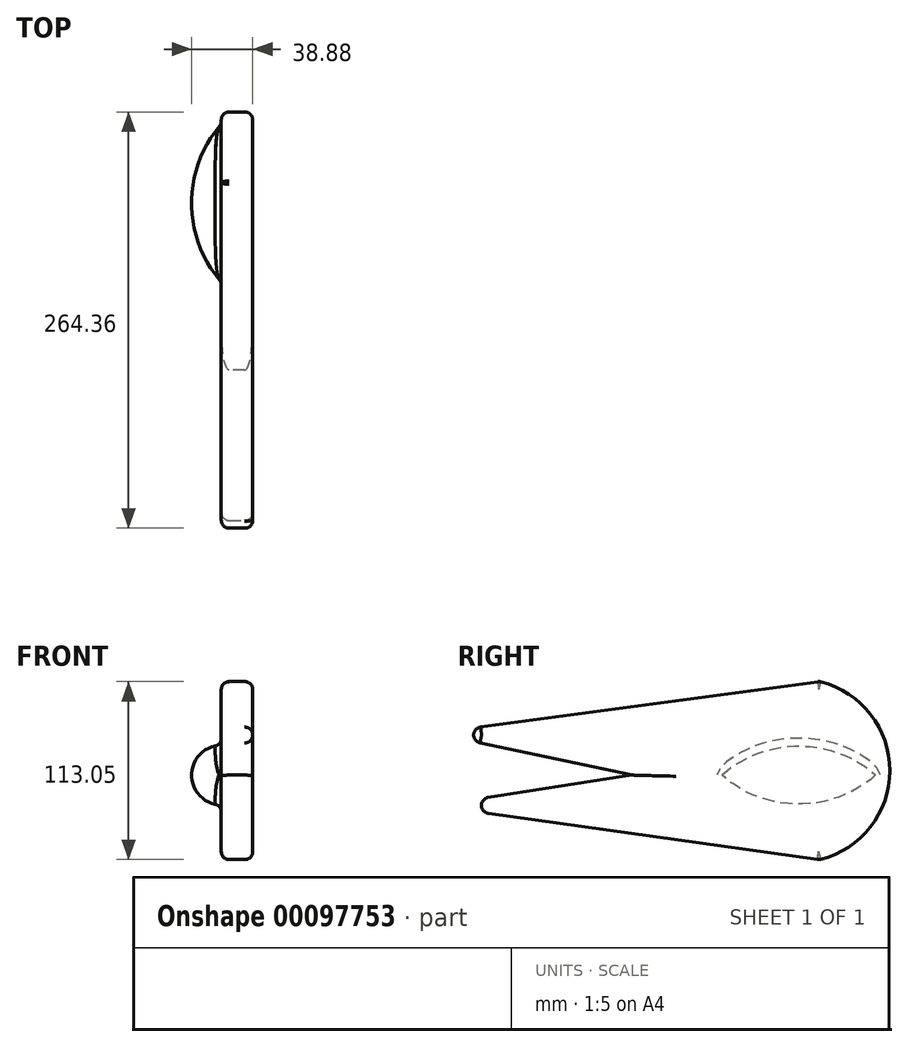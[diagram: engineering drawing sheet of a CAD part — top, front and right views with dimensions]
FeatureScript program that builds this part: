
annotation { "Feature Type Name" : "Feature", "Feature Type Description" : "" }
export const myFeature = defineFeature(function(context is Context, id is Id, definition is map)
    precondition{}
    {
        {
            var Q0;
            Q0=qCreatedBy(makeId("Right.planeOp"),FACE);
            var sketch = newSketch(context, id + "F0", { "sketchPlane" : qUnion([Q0])});
            skLineSegment(sketch, "E0", {"start": v(118.87, -53.77) * mm, "end": v(-125.11, -19.52) * mm});
            skLineSegment(sketch, "E1", {"start": v(119.06, 59.45) * mm, "end": v(-125.11, 26.58) * mm});
            skLineSegment(sketch, "E2", {"start": v(-125.11, 26.58) * mm, "end": v(0, 0) * mm});
            skLineSegment(sketch, "E3", {"start": v(0, 0) * mm, "end": v(-125.11, -19.52) * mm});
            skArc(sketch, "E4", {"start": v(118.87, -53.77) * mm, "mid": v(163.9, 2.76) * mm, "end": v(119.06, 59.45) * mm});
            skSolve(sketch);
        }
        {
            var Q0;
            Q0=makeQuery(id+"F0.imprint","IMPRINT",FACE,{"disambiguationData":[TD([[makeQuery(id+"F0.imprint","IMPRINT",EDGE,{"derivedFrom":sQuery(id+"F0.wireOp",EDGE,"E0")}),-1.0]])]});
            extrude(context, id + "F1", {"entities" : qUnion([Q0]), "depth" : 20 * mm});
        }
        {
            var Q0;
            Q0=makeQuery(id+"F1.opExtrude","SWEPT_EDGE",EDGE,{"disambiguationData":[OSD([sQuery(id+"F0.wireOp",EDGE,"E0"),sQuery(id+"F0.wireOp",EDGE,"E3")])]});
            var Q1;
            Q1=makeQuery(id+"F1.opExtrude","SWEPT_EDGE",EDGE,{"disambiguationData":[OSD([sQuery(id+"F0.wireOp",EDGE,"E1"),sQuery(id+"F0.wireOp",EDGE,"E2")])]});
            var Q2;
            Q2=makeQuery(id+"F1.opExtrude","CAP_EDGE",EDGE,{"disambiguationData":[OSD([sQuery(id+"F0.wireOp",EDGE,"E1")])],"isStart":true});
            var Q3;
            Q3=makeQuery(id+"F1.opExtrude","CAP_EDGE",EDGE,{"disambiguationData":[OSD([sQuery(id+"F0.wireOp",EDGE,"E2")])],"isStart":true});
            var Q4;
            Q4=makeQuery(id+"F1.opExtrude","CAP_EDGE",EDGE,{"disambiguationData":[OSD([sQuery(id+"F0.wireOp",EDGE,"E3")])],"isStart":true});
            var Q5;
            Q5=makeQuery(id+"F1.opExtrude","CAP_EDGE",EDGE,{"disambiguationData":[OSD([sQuery(id+"F0.wireOp",EDGE,"E0")])],"isStart":true});
            var Q6;
            Q6=makeQuery(id+"F1.opExtrude","CAP_EDGE",EDGE,{"disambiguationData":[OSD([sQuery(id+"F0.wireOp",EDGE,"E3")])],"isStart":false});
            var Q7;
            Q7=makeQuery(id+"F1.opExtrude","CAP_EDGE",EDGE,{"disambiguationData":[OSD([sQuery(id+"F0.wireOp",EDGE,"E1")])],"isStart":false});
            var Q8;
            Q8=makeQuery(id+"F1.opExtrude","CAP_EDGE",EDGE,{"disambiguationData":[OSD([sQuery(id+"F0.wireOp",EDGE,"E0")])],"isStart":false});
            var Q9;
            Q9=makeQuery(id+"F1.opExtrude","CAP_EDGE",EDGE,{"disambiguationData":[OSD([sQuery(id+"F0.wireOp",EDGE,"E4")])],"isStart":false});
            var Q10;
            Q10=makeQuery(id+"F1.opExtrude","SWEPT_EDGE",EDGE,{"disambiguationData":[OSD([sQuery(id+"F0.wireOp",EDGE,"E0"),sQuery(id+"F0.wireOp",EDGE,"E4")])]});
            var Q11;
            Q11=makeQuery(id+"F1.opExtrude","SWEPT_EDGE",EDGE,{"disambiguationData":[OSD([sQuery(id+"F0.wireOp",EDGE,"E1"),sQuery(id+"F0.wireOp",EDGE,"E4")])]});
            fillet(context, id + "F2", {"entities" : qUnion([Q0, Q1, Q2, Q3, Q4, Q5, Q6, Q7, Q8, Q9, Q10, Q11]), "radius" : 5.08 * mm, "tangentPropagation" : true, "allowEdgeOverflow" : false});
        }
        {
            var Q0;
            Q0=makeQuery(id+"F1.opExtrude","CAP_FACE",FACE,{"disambiguationData":[OSD([sQuery(id+"F0.wireOp",EDGE,"E0"),sQuery(id+"F0.wireOp",EDGE,"E1"),sQuery(id+"F0.wireOp",EDGE,"E2"),sQuery(id+"F0.wireOp",EDGE,"E3"),sQuery(id+"F0.wireOp",EDGE,"E4")])],"isStart":true});
            var sketch = newSketch(context, id + "F3", { "sketchPlane" : qUnion([Q0])});
            skArc(sketch, "E5", {"start": v(-156.16, 0) * mm, "mid": v(-106.02, -18.88) * mm, "end": v(-55.88, 0) * mm});
            skLineSegment(sketch, "E6", {"start": v(-156.16, 0) * mm, "end": v(-55.88, 0) * mm});
            skSolve(sketch);
        }
        {
            var Q0;
            Q0=makeQuery(id+"F3.imprint","IMPRINT",FACE,{"disambiguationData":[TD([[makeQuery(id+"F3.imprint","IMPRINT",EDGE,{"derivedFrom":sQuery(id+"F3.wireOp",EDGE,"E5")}),1.0]])]});
            var Q1;
            Q1=sQuery(id+"F3.wireOp",EDGE,"E6");
            revolve(context, id + "F4", {"operationType" : NewBodyOperationType.ADD, "entities" : qUnion([Q0]), "axis" : qUnion([Q1]), "revolveType" : RevolveType.ONE_DIRECTION, "oppositeDirection" : true, "angle" : 180 * degree});
        }
        {
            var Q0;
            Q0=makeQuery(id+"F4.opRevolve","CAP_EDGE",EDGE,{"disambiguationData":[OSD([sQuery(id+"F3.wireOp",EDGE,"E5")])],"isStart":false});
            var Q1;
            Q1=makeQuery(id+"F4.opRevolve","CAP_EDGE",EDGE,{"disambiguationData":[OSD([sQuery(id+"F3.wireOp",EDGE,"E5")])],"isStart":true});
            var Q2;
            Q2=makeQuery(id+"F4.opRevolve","SWEPT_FACE",FACE,{"disambiguationData":[OSD([sQuery(id+"F3.wireOp",EDGE,"E5")])]});
            fillet(context, id + "F5", {"entities" : qUnion([Q0, Q1, Q2]), "radius" : 5.08 * mm, "tangentPropagation" : true, "allowEdgeOverflow" : false});
        }
        {
            var Q0;
            Q0=makeQuery(id+"F1.opExtrude","CAP_EDGE",EDGE,{"disambiguationData":[OSD([sQuery(id+"F0.wireOp",EDGE,"E4")])],"isStart":true});
            var Q1;
            {var subQ0=sQuery(id+"F0.wireOp",EDGE,"E4");Q1=makeQuery(id+"F2.opFillet","BLEND_EDGE",EDGE,{"blendedFrom":[makeQuery(id+"F1.opExtrude","CAP_EDGE",EDGE,{"disambiguationData":[OSD([subQ0])],"isStart":false}),makeQuery(id+"F1.opExtrude","SWEPT_FACE",FACE,{"disambiguationData":[OSD([subQ0])]})],"blendedInto":[makeQuery(id+"F1.opExtrude","SWEPT_FACE",FACE,{"disambiguationData":[OSD([subQ0])]})]});}
            var Q2;
            Q2=makeQuery(id+"F1.opExtrude","CAP_EDGE",EDGE,{"disambiguationData":[OSD([sQuery(id+"F0.wireOp",EDGE,"E2")])],"isStart":false});
            var Q3;
            {var subQ0=sQuery(id+"F0.wireOp",EDGE,"E3");Q3=makeQuery(id+"F2.opFillet","BLEND_EDGE",EDGE,{"blendedFrom":[makeQuery(id+"F1.opExtrude","CAP_EDGE",EDGE,{"disambiguationData":[OSD([subQ0])],"isStart":false}),makeQuery(id+"F1.opExtrude","CAP_FACE",FACE,{"disambiguationData":[OSD([sQuery(id+"F0.wireOp",EDGE,"E0"),sQuery(id+"F0.wireOp",EDGE,"E1"),sQuery(id+"F0.wireOp",EDGE,"E2"),subQ0,sQuery(id+"F0.wireOp",EDGE,"E4")])],"isStart":false})],"blendedInto":[makeQuery(id+"F1.opExtrude","CAP_FACE",FACE,{"disambiguationData":[OSD([sQuery(id+"F0.wireOp",EDGE,"E0"),sQuery(id+"F0.wireOp",EDGE,"E1"),sQuery(id+"F0.wireOp",EDGE,"E2"),subQ0,sQuery(id+"F0.wireOp",EDGE,"E4")])],"isStart":false})]});}
            var Q4;
            {var subQ0=sQuery(id+"F0.wireOp",EDGE,"E3");Q4=makeQuery(id+"F2.opFillet","BLEND_EDGE",EDGE,{"blendedFrom":[makeQuery(id+"F1.opExtrude","CAP_EDGE",EDGE,{"disambiguationData":[OSD([subQ0])],"isStart":true}),makeQuery(id+"F1.opExtrude","SWEPT_FACE",FACE,{"disambiguationData":[OSD([subQ0])]})],"blendedInto":[makeQuery(id+"F1.opExtrude","SWEPT_FACE",FACE,{"disambiguationData":[OSD([subQ0])]})]});}
            var Q5;
            {var subQ0=sQuery(id+"F0.wireOp",EDGE,"E2");Q5=makeQuery(id+"F2.opFillet","BLEND_EDGE",EDGE,{"blendedFrom":[makeQuery(id+"F1.opExtrude","CAP_EDGE",EDGE,{"disambiguationData":[OSD([subQ0])],"isStart":true}),makeQuery(id+"F1.opExtrude","SWEPT_FACE",FACE,{"disambiguationData":[OSD([subQ0])]})],"blendedInto":[makeQuery(id+"F1.opExtrude","SWEPT_FACE",FACE,{"disambiguationData":[OSD([subQ0])]})]});}
            var Q6;
            {var subQ0=sQuery(id+"F0.wireOp",EDGE,"E2");Q6=makeQuery(id+"F2.opFillet","BLEND_EDGE",EDGE,{"blendedFrom":[makeQuery(id+"F1.opExtrude","CAP_EDGE",EDGE,{"disambiguationData":[OSD([subQ0])],"isStart":true}),makeQuery(id+"F1.opExtrude","CAP_FACE",FACE,{"disambiguationData":[OSD([sQuery(id+"F0.wireOp",EDGE,"E0"),sQuery(id+"F0.wireOp",EDGE,"E1"),subQ0,sQuery(id+"F0.wireOp",EDGE,"E3"),sQuery(id+"F0.wireOp",EDGE,"E4")])],"isStart":true})],"blendedInto":[makeQuery(id+"F1.opExtrude","CAP_FACE",FACE,{"disambiguationData":[OSD([sQuery(id+"F0.wireOp",EDGE,"E0"),sQuery(id+"F0.wireOp",EDGE,"E1"),subQ0,sQuery(id+"F0.wireOp",EDGE,"E3"),sQuery(id+"F0.wireOp",EDGE,"E4")])],"isStart":true})]});}
            var Q7;
            {var subQ0=sQuery(id+"F0.wireOp",EDGE,"E3");Q7=makeQuery(id+"F2.opFillet","BLEND_EDGE",EDGE,{"blendedFrom":[makeQuery(id+"F1.opExtrude","CAP_EDGE",EDGE,{"disambiguationData":[OSD([subQ0])],"isStart":true}),makeQuery(id+"F1.opExtrude","CAP_FACE",FACE,{"disambiguationData":[OSD([sQuery(id+"F0.wireOp",EDGE,"E0"),sQuery(id+"F0.wireOp",EDGE,"E1"),sQuery(id+"F0.wireOp",EDGE,"E2"),subQ0,sQuery(id+"F0.wireOp",EDGE,"E4")])],"isStart":true})],"blendedInto":[makeQuery(id+"F1.opExtrude","CAP_FACE",FACE,{"disambiguationData":[OSD([sQuery(id+"F0.wireOp",EDGE,"E0"),sQuery(id+"F0.wireOp",EDGE,"E1"),sQuery(id+"F0.wireOp",EDGE,"E2"),subQ0,sQuery(id+"F0.wireOp",EDGE,"E4")])],"isStart":true})]});}
            var Q8;
            {var subQ0=sQuery(id+"F0.wireOp",EDGE,"E3");Q8=makeQuery(id+"F2.opFillet","BLEND_EDGE",EDGE,{"blendedFrom":[makeQuery(id+"F1.opExtrude","CAP_EDGE",EDGE,{"disambiguationData":[OSD([subQ0])],"isStart":false}),makeQuery(id+"F1.opExtrude","SWEPT_FACE",FACE,{"disambiguationData":[OSD([subQ0])]})],"blendedInto":[makeQuery(id+"F1.opExtrude","SWEPT_FACE",FACE,{"disambiguationData":[OSD([subQ0])]})]});}
            fillet(context, id + "F6", {"entities" : qUnion([Q0, Q1, Q2, Q3, Q4, Q5, Q6, Q7, Q8]), "radius" : 5.08 * mm, "tangentPropagation" : true, "allowEdgeOverflow" : false});
        }
    });
